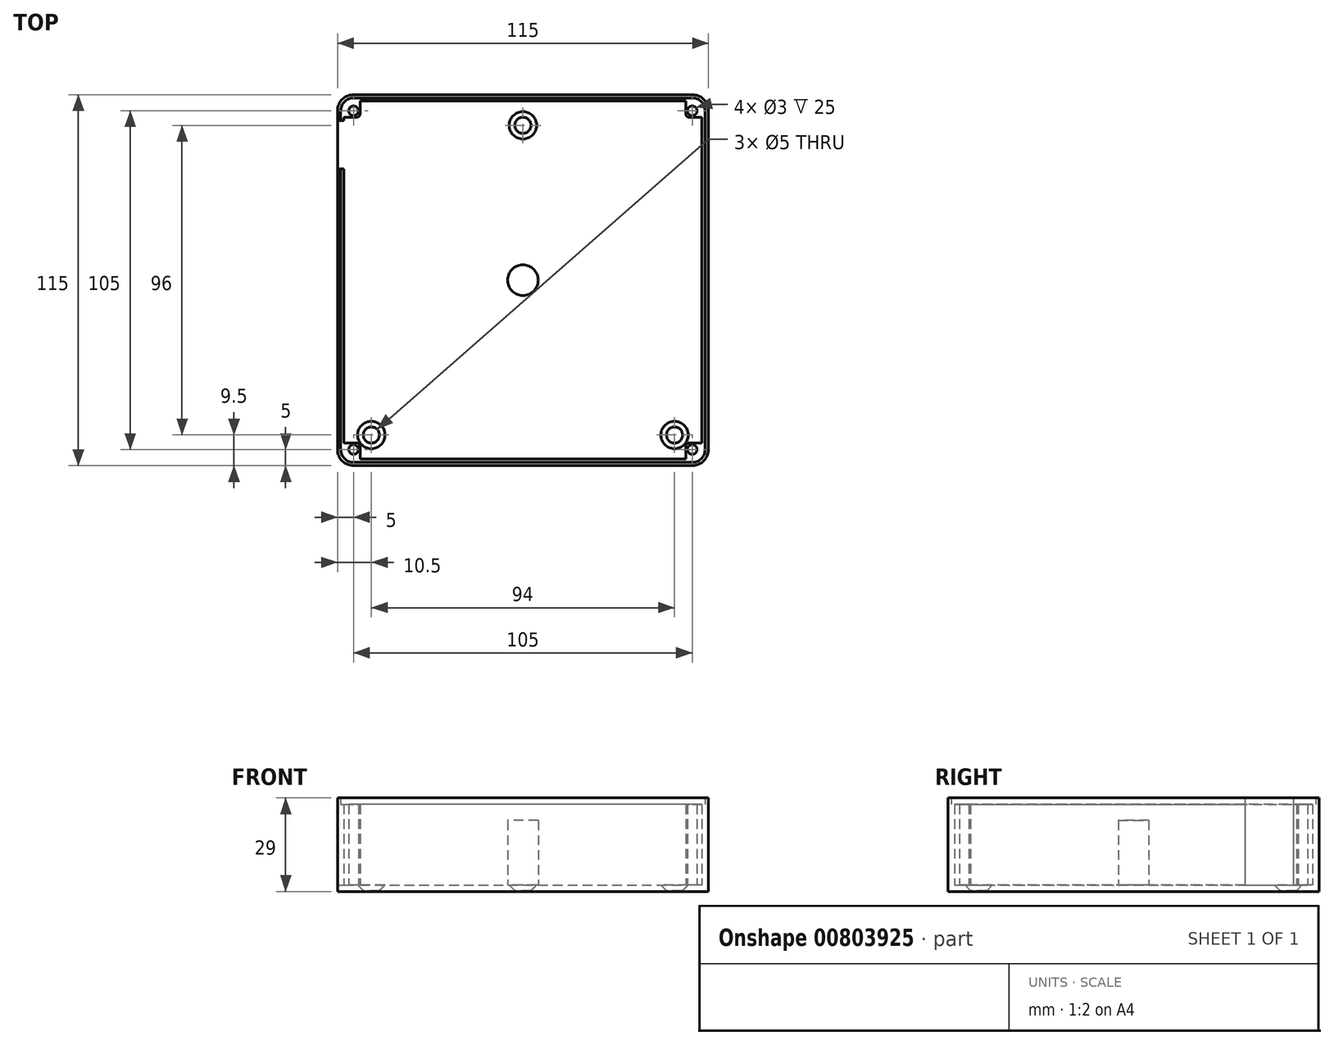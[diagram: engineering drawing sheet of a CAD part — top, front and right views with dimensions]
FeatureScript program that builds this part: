
annotation { "Feature Type Name" : "Feature", "Feature Type Description" : "" }
export const myFeature = defineFeature(function(context is Context, id is Id, definition is map)
    precondition{}
    {
        {
            var Q0;
            Q0=qCreatedBy(makeId("Top.planeOp"),FACE);
            var sketch = newSketch(context, id + "F0", { "sketchPlane" : qUnion([Q0])});
            skLineSegment(sketch, "E0.bottom", {"start": v(-52.5, -57.5) * mm, "end": v(52.5, -57.5) * mm});
            skLineSegment(sketch, "E0.top", {"start": v(-52.5, 57.5) * mm, "end": v(52.5, 57.5) * mm});
            skLineSegment(sketch, "E0.left", {"start": v(-57.5, -52.5) * mm, "end": v(-57.5, 52.5) * mm});
            skLineSegment(sketch, "E0.right", {"start": v(57.5, -52.5) * mm, "end": v(57.5, 52.5) * mm});
            skPoint(sketch, "E1.visualSharp", {"position": v(-57.5, 57.5) * mm});
            skArc(sketch, "E1.filletArc", {"start": v(-52.5, 57.5) * mm, "mid": v(-56.04, 56.04) * mm, "end": v(-57.5, 52.5) * mm});
            skPoint(sketch, "E2.visualSharp", {"position": v(57.5, 57.5) * mm});
            skArc(sketch, "E2.filletArc", {"start": v(57.5, 52.5) * mm, "mid": v(56.04, 56.04) * mm, "end": v(52.5, 57.5) * mm});
            skPoint(sketch, "E3.visualSharp", {"position": v(57.5, -57.5) * mm});
            skArc(sketch, "E3.filletArc", {"start": v(52.5, -57.5) * mm, "mid": v(56.04, -56.04) * mm, "end": v(57.5, -52.5) * mm});
            skPoint(sketch, "E4.visualSharp", {"position": v(-57.5, -57.5) * mm});
            skArc(sketch, "E4.filletArc", {"start": v(-57.5, -52.5) * mm, "mid": v(-56.04, -56.04) * mm, "end": v(-52.5, -57.5) * mm});
            skLineSegment(sketch, "E5", {"start": v(-57.5, 57.5) * mm, "end": v(57.5, -57.5) * mm, "construction": true});
            skLineSegment(sketch, "E6", {"start": v(-57.5, -57.5) * mm, "end": v(57.5, 57.5) * mm, "construction": true});
            skSolve(sketch);
        }
        {
            var Q0;
            Q0 = qSketchRegion(id + "F0", true);
            extrude(context, id + "F1", {"entities" : qUnion([Q0]), "depth" : 2 * mm, "offsetDistance" : 25 * mm});
        }
        {
            var Q0;
            Q0=makeQuery(id+"F1.opExtrude","CAP_FACE",FACE,{"disambiguationData":[OSD([sQuery(id+"F0.wireOp",EDGE,"E0.bottom"),sQuery(id+"F0.wireOp",EDGE,"E0.top"),sQuery(id+"F0.wireOp",EDGE,"E0.left"),sQuery(id+"F0.wireOp",EDGE,"E0.right"),sQuery(id+"F0.wireOp",EDGE,"E1.filletArc"),sQuery(id+"F0.wireOp",EDGE,"E2.filletArc"),sQuery(id+"F0.wireOp",EDGE,"E3.filletArc"),sQuery(id+"F0.wireOp",EDGE,"E4.filletArc")])],"isStart":false});
            var sketch = newSketch(context, id + "F2", { "sketchPlane" : qUnion([Q0])});
            skCircle(sketch, "E7", {"center": v(0, 0) * mm, "radius": 4.75 * mm});
            skLineSegment(sketch, "E8", {"start": v(-55.5, 50.5) * mm, "end": v(-55.5, 49.5) * mm});
            skPoint(sketch, "E8.startSnap0", {"position": v(-56.04, 56.04) * mm});
            skLineSegment(sketch, "E9", {"start": v(-50.5, -55.5) * mm, "end": v(50.5, -55.5) * mm});
            skPoint(sketch, "E9.startSnap0", {"position": v(-56.04, -56.04) * mm});
            skLineSegment(sketch, "E10", {"start": v(55.5, -50.5) * mm, "end": v(55.5, 50.5) * mm});
            skPoint(sketch, "E10.startSnap0", {"position": v(56.04, -56.04) * mm});
            skLineSegment(sketch, "E11", {"start": v(50.5, 55.5) * mm, "end": v(-50.5, 55.5) * mm});
            skPoint(sketch, "E11.startSnap0", {"position": v(56.04, 56.04) * mm});
            skLineSegment(sketch, "E12", {"start": v(-57.5, 49.5) * mm, "end": v(-55.5, 49.5) * mm});
            skLineSegment(sketch, "E13", {"start": v(-57.5, 34.5) * mm, "end": v(-55.5, 34.5) * mm});
            skLineSegment(sketch, "E14.trimOffspring", {"start": v(-55.5, 34.5) * mm, "end": v(-55.5, -50.5) * mm});
            skCircle(sketch, "E15", {"center": v(0, 48) * mm, "radius": 2.5 * mm});
            skCircle(sketch, "E16", {"center": v(-47, -48) * mm, "radius": 2.5 * mm});
            skCircle(sketch, "E17", {"center": v(47, -48) * mm, "radius": 2.5 * mm});
            skLineSegment(sketch, "E18.0", {"start": v(57.5, -52.5) * mm, "end": v(57.5, 52.5) * mm});
            skArc(sketch, "E19.0", {"start": v(57.5, 52.5) * mm, "mid": v(56.04, 56.04) * mm, "end": v(52.5, 57.5) * mm});
            skLineSegment(sketch, "E20.0", {"start": v(-52.5, 57.5) * mm, "end": v(52.5, 57.5) * mm});
            skArc(sketch, "E21.0", {"start": v(-52.5, 57.5) * mm, "mid": v(-56.04, 56.04) * mm, "end": v(-57.5, 52.5) * mm});
            skLineSegment(sketch, "E22.0", {"start": v(-57.5, -52.5) * mm, "end": v(-57.5, 34.5) * mm});
            skArc(sketch, "E23.0", {"start": v(-57.5, -52.5) * mm, "mid": v(-56.04, -56.04) * mm, "end": v(-52.5, -57.5) * mm});
            skLineSegment(sketch, "E24.0", {"start": v(-52.5, -57.5) * mm, "end": v(52.5, -57.5) * mm});
            skLineSegment(sketch, "E25.trimOffspring", {"start": v(-57.5, 49.5) * mm, "end": v(-57.5, 52.5) * mm});
            skArc(sketch, "E26.0", {"start": v(52.5, -57.5) * mm, "mid": v(56.04, -56.04) * mm, "end": v(57.5, -52.5) * mm});
            skLineSegment(sketch, "E27", {"start": v(-50.5, 55.5) * mm, "end": v(-50.5, 51.5) * mm});
            skLineSegment(sketch, "E28", {"start": v(-55.5, 50.5) * mm, "end": v(-51.5, 50.5) * mm});
            skPoint(sketch, "E29.visualSharp", {"position": v(-50.5, 50.5) * mm});
            skArc(sketch, "E29.filletArc", {"start": v(-51.5, 50.5) * mm, "mid": v(-50.8, 50.8) * mm, "end": v(-50.5, 51.5) * mm});
            skLineSegment(sketch, "E30", {"start": v(50.5, 55.5) * mm, "end": v(50.5, 51.5) * mm});
            skLineSegment(sketch, "E31", {"start": v(55.5, 50.5) * mm, "end": v(51.5, 50.5) * mm});
            skPoint(sketch, "E32.visualSharp", {"position": v(50.5, 50.5) * mm});
            skArc(sketch, "E32.filletArc", {"start": v(50.5, 51.5) * mm, "mid": v(50.8, 50.8) * mm, "end": v(51.5, 50.5) * mm});
            skLineSegment(sketch, "E33", {"start": v(50.5, -55.5) * mm, "end": v(50.5, -51.5) * mm});
            skLineSegment(sketch, "E34", {"start": v(55.5, -50.5) * mm, "end": v(51.5, -50.5) * mm});
            skPoint(sketch, "E35.visualSharp", {"position": v(50.5, -50.5) * mm});
            skArc(sketch, "E35.filletArc", {"start": v(51.5, -50.5) * mm, "mid": v(50.8, -50.8) * mm, "end": v(50.5, -51.5) * mm});
            skLineSegment(sketch, "E36", {"start": v(-55.5, -50.5) * mm, "end": v(-51.5, -50.5) * mm});
            skLineSegment(sketch, "E37", {"start": v(-50.5, -55.5) * mm, "end": v(-50.5, -51.5) * mm});
            skPoint(sketch, "E38.visualSharp", {"position": v(-50.5, -50.5) * mm});
            skArc(sketch, "E38.filletArc", {"start": v(-50.5, -51.5) * mm, "mid": v(-50.8, -50.8) * mm, "end": v(-51.5, -50.5) * mm});
            skCircle(sketch, "E39", {"center": v(-52.5, -52.5) * mm, "radius": 1.5 * mm});
            skCircle(sketch, "E40", {"center": v(52.5, -52.5) * mm, "radius": 1.5 * mm});
            skCircle(sketch, "E41", {"center": v(52.5, 52.5) * mm, "radius": 1.5 * mm});
            skCircle(sketch, "E42", {"center": v(-52.5, 52.5) * mm, "radius": 1.5 * mm});
            skSolve(sketch);
        }
        {
            var Q0;
            Q0=makeQuery(id+"F2.imprint","IMPRINT",FACE,{"disambiguationData":[TD([[makeQuery(id+"F2.imprint","IMPRINT",EDGE,{"derivedFrom":sQuery(id+"F2.wireOp",EDGE,"E7")}),1.0]])]});
            extrude(context, id + "F3", {"entities" : qUnion([Q0]), "operationType" : NewBodyOperationType.ADD, "depth" : 20 * mm, "offsetDistance" : 25 * mm});
        }
        {
            var Q0;
            Q0=makeQuery(id+"F2.imprint","IMPRINT",FACE,{"disambiguationData":[TD([[makeQuery(id+"F2.imprint","IMPRINT",EDGE,{"derivedFrom":sQuery(id+"F2.wireOp",EDGE,"E17")}),1.0]])]});
            var Q1;
            Q1=makeQuery(id+"F2.imprint","IMPRINT",FACE,{"disambiguationData":[TD([[makeQuery(id+"F2.imprint","IMPRINT",EDGE,{"derivedFrom":sQuery(id+"F2.wireOp",EDGE,"E15")}),1.0]])]});
            var Q2;
            Q2=makeQuery(id+"F2.imprint","IMPRINT",FACE,{"disambiguationData":[TD([[makeQuery(id+"F2.imprint","IMPRINT",EDGE,{"derivedFrom":sQuery(id+"F2.wireOp",EDGE,"E16")}),1.0]])]});
            extrude(context, id + "F4", {"entities" : qUnion([Q0, Q1, Q2]), "operationType" : NewBodyOperationType.REMOVE, "oppositeDirection" : true, "depth" : 2 * mm, "offsetDistance" : 25 * mm});
        }
        {
            var Q0;
            Q0=makeQuery(id+"F2.imprint","IMPRINT",FACE,{"disambiguationData":[TD([[makeQuery(id+"F2.imprint","IMPRINT",EDGE,{"derivedFrom":sQuery(id+"F2.wireOp",EDGE,"E8")}),-1.0]])]});
            extrude(context, id + "F5", {"entities" : qUnion([Q0]), "operationType" : NewBodyOperationType.ADD, "depth" : 25 * mm, "offsetDistance" : 25 * mm});
        }
        {
            var Q0;
            Q0=makeQuery(id+"F5.opExtrude","CAP_FACE",FACE,{"disambiguationData":[OSD([sQuery(id+"F2.wireOp",EDGE,"E8"),sQuery(id+"F2.wireOp",EDGE,"E9"),sQuery(id+"F2.wireOp",EDGE,"E10"),sQuery(id+"F2.wireOp",EDGE,"E11"),sQuery(id+"F2.wireOp",EDGE,"E12"),sQuery(id+"F2.wireOp",EDGE,"E13"),sQuery(id+"F2.wireOp",EDGE,"E14.trimOffspring"),sQuery(id+"F2.wireOp",EDGE,"E18.0"),sQuery(id+"F2.wireOp",EDGE,"E19.0"),sQuery(id+"F2.wireOp",EDGE,"E20.0"),sQuery(id+"F2.wireOp",EDGE,"E21.0"),sQuery(id+"F2.wireOp",EDGE,"E22.0"),sQuery(id+"F2.wireOp",EDGE,"E23.0"),sQuery(id+"F2.wireOp",EDGE,"E24.0"),sQuery(id+"F2.wireOp",EDGE,"E25.trimOffspring"),sQuery(id+"F2.wireOp",EDGE,"E26.0"),sQuery(id+"F2.wireOp",EDGE,"E27"),sQuery(id+"F2.wireOp",EDGE,"E28"),sQuery(id+"F2.wireOp",EDGE,"E29.filletArc"),sQuery(id+"F2.wireOp",EDGE,"E30"),sQuery(id+"F2.wireOp",EDGE,"E31"),sQuery(id+"F2.wireOp",EDGE,"E32.filletArc"),sQuery(id+"F2.wireOp",EDGE,"E33"),sQuery(id+"F2.wireOp",EDGE,"E34"),sQuery(id+"F2.wireOp",EDGE,"E35.filletArc"),sQuery(id+"F2.wireOp",EDGE,"E36"),sQuery(id+"F2.wireOp",EDGE,"E37"),sQuery(id+"F2.wireOp",EDGE,"E38.filletArc"),sQuery(id+"F2.wireOp",EDGE,"E39"),sQuery(id+"F2.wireOp",EDGE,"E40"),sQuery(id+"F2.wireOp",EDGE,"E41"),sQuery(id+"F2.wireOp",EDGE,"E42")])],"isStart":false});
            var sketch = newSketch(context, id + "F6", { "sketchPlane" : qUnion([Q0])});
            skArc(sketch, "E43.0", {"start": v(-52.5, 57.5) * mm, "mid": v(-56.04, 56.04) * mm, "end": v(-57.5, 52.5) * mm});
            skArc(sketch, "E43.1", {"start": v(57.5, 52.5) * mm, "mid": v(56.04, 56.04) * mm, "end": v(52.5, 57.5) * mm});
            skLineSegment(sketch, "E43.2", {"start": v(-52.5, 57.5) * mm, "end": v(52.5, 57.5) * mm});
            skLineSegment(sketch, "E43.3", {"start": v(-57.5, 49.5) * mm, "end": v(-57.5, 52.5) * mm});
            skLineSegment(sketch, "E43.4", {"start": v(57.5, -52.5) * mm, "end": v(57.5, 52.5) * mm});
            skArc(sketch, "E43.5", {"start": v(52.5, -57.5) * mm, "mid": v(56.04, -56.04) * mm, "end": v(57.5, -52.5) * mm});
            skLineSegment(sketch, "E43.6", {"start": v(-52.5, -57.5) * mm, "end": v(52.5, -57.5) * mm});
            skArc(sketch, "E43.7", {"start": v(-57.5, -52.5) * mm, "mid": v(-56.04, -56.04) * mm, "end": v(-52.5, -57.5) * mm});
            skLineSegment(sketch, "E43.8", {"start": v(-57.5, -52.5) * mm, "end": v(-57.5, 34.5) * mm});
            skLineSegment(sketch, "E44", {"start": v(-56.5, 49.5) * mm, "end": v(-56.5, 52.5) * mm});
            skLineSegment(sketch, "E45", {"start": v(-52.5, 56.5) * mm, "end": v(52.5, 56.5) * mm});
            skLineSegment(sketch, "E46", {"start": v(56.5, 52.5) * mm, "end": v(56.5, -52.5) * mm});
            skLineSegment(sketch, "E47", {"start": v(52.5, -56.5) * mm, "end": v(-52.5, -56.5) * mm});
            skLineSegment(sketch, "E48", {"start": v(-56.5, -52.5) * mm, "end": v(-56.5, 34.5) * mm});
            skArc(sketch, "E49", {"start": v(-52.5, 56.5) * mm, "mid": v(-55.33, 55.33) * mm, "end": v(-56.5, 52.5) * mm});
            skArc(sketch, "E50", {"start": v(56.5, 52.5) * mm, "mid": v(55.33, 55.33) * mm, "end": v(52.5, 56.5) * mm});
            skArc(sketch, "E51", {"start": v(52.5, -56.5) * mm, "mid": v(55.33, -55.33) * mm, "end": v(56.5, -52.5) * mm});
            skArc(sketch, "E52", {"start": v(-56.5, -52.5) * mm, "mid": v(-55.33, -55.33) * mm, "end": v(-52.5, -56.5) * mm});
            skSolve(sketch);
        }
        {
            var Q0;
            Q0 = qSketchRegion(id + "F6", true);
            var Q1;
            Q1=makeQuery(id+"F6.imprint","IMPRINT",FACE,{"disambiguationData":[TD([[makeQuery(id+"F6.imprint","IMPRINT",EDGE,{"derivedFrom":sQuery(id+"F6.wireOp",EDGE,"E43.0")}),1.0]])]});
            extrude(context, id + "F7", {"entities" : qUnion([Q0, Q1]), "operationType" : NewBodyOperationType.ADD, "depth" : 2 * mm, "offsetDistance" : 25 * mm});
        }
        {
            var Q0;
            Q0=sQuery(id+"F2.wireOp",VERTEX,"E15.center");
            var Q1;
            Q1=makeQuery(id+"F1.opExtrude","SWEPT_BODY",BODY,{"disambiguationData":[OSD([sQuery(id+"F0.wireOp",EDGE,"E0.bottom"),sQuery(id+"F0.wireOp",EDGE,"E0.top"),sQuery(id+"F0.wireOp",EDGE,"E0.left"),sQuery(id+"F0.wireOp",EDGE,"E0.right"),sQuery(id+"F0.wireOp",EDGE,"E1.filletArc"),sQuery(id+"F0.wireOp",EDGE,"E2.filletArc"),sQuery(id+"F0.wireOp",EDGE,"E3.filletArc"),sQuery(id+"F0.wireOp",EDGE,"E4.filletArc")])]});
            hole(context, id + "F8", {"style" : HoleStyle.C_SINK, "endStyle" : HoleEndStyle.THROUGH, "holeDiameter" : 5 * mm, "cSinkDiameter" : 8.5 * mm, "cSinkAngle" : 90 * degree, "majorDiameter" : 5 * mm, "isTappedThrough" : true, "tappedDepth" : 12 * mm, "tapClearance" : 3, "locations" : qUnion([Q0]), "scope" : qUnion([Q1])});
        }
        {
            var Q0;
            Q0=sQuery(id+"F2.wireOp",VERTEX,"E17.center");
            var Q1;
            Q1=makeQuery(id+"F1.opExtrude","SWEPT_BODY",BODY,{"disambiguationData":[OSD([sQuery(id+"F0.wireOp",EDGE,"E0.bottom"),sQuery(id+"F0.wireOp",EDGE,"E0.top"),sQuery(id+"F0.wireOp",EDGE,"E0.left"),sQuery(id+"F0.wireOp",EDGE,"E0.right"),sQuery(id+"F0.wireOp",EDGE,"E1.filletArc"),sQuery(id+"F0.wireOp",EDGE,"E2.filletArc"),sQuery(id+"F0.wireOp",EDGE,"E3.filletArc"),sQuery(id+"F0.wireOp",EDGE,"E4.filletArc")])]});
            hole(context, id + "F9", {"style" : HoleStyle.C_SINK, "endStyle" : HoleEndStyle.THROUGH, "holeDiameter" : 5 * mm, "cSinkDiameter" : 8.5 * mm, "cSinkAngle" : 90 * degree, "majorDiameter" : 5 * mm, "isTappedThrough" : true, "tappedDepth" : 12 * mm, "tapClearance" : 3, "locations" : qUnion([Q0]), "scope" : qUnion([Q1])});
        }
        {
            var Q0;
            Q0=sQuery(id+"F2.wireOp",VERTEX,"E16.center");
            var Q1;
            Q1=makeQuery(id+"F1.opExtrude","SWEPT_BODY",BODY,{"disambiguationData":[OSD([sQuery(id+"F0.wireOp",EDGE,"E0.bottom"),sQuery(id+"F0.wireOp",EDGE,"E0.top"),sQuery(id+"F0.wireOp",EDGE,"E0.left"),sQuery(id+"F0.wireOp",EDGE,"E0.right"),sQuery(id+"F0.wireOp",EDGE,"E1.filletArc"),sQuery(id+"F0.wireOp",EDGE,"E2.filletArc"),sQuery(id+"F0.wireOp",EDGE,"E3.filletArc"),sQuery(id+"F0.wireOp",EDGE,"E4.filletArc")])]});
            hole(context, id + "F10", {"style" : HoleStyle.C_SINK, "endStyle" : HoleEndStyle.THROUGH, "holeDiameter" : 5 * mm, "cSinkDiameter" : 8.5 * mm, "cSinkAngle" : 90 * degree, "majorDiameter" : 5 * mm, "isTappedThrough" : true, "tappedDepth" : 12 * mm, "tapClearance" : 3, "locations" : qUnion([Q0]), "scope" : qUnion([Q1])});
        }
    });
